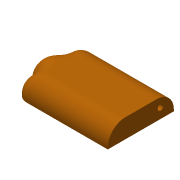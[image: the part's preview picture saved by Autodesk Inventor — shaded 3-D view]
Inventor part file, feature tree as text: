
AUTODESK INVENTOR PART (.ipt)
format: ipt  version: 2016 (Build 200138000, 138)  size: 172,032 bytes
history: native  units: in
note: dims shown in document units (in); Inventor stores cm internally (conversion verified against a paired STEP export)
features: sketch x4, other x3, plane x1
ambient origin geometry x8: Origin, YZ Plane, XZ Plane, XY Plane, X Axis, Y Axis, Z Axis, Center Point
bodies: Solid1 (feature_tree)
feature tree (8):
  other  "P_ankle03_001.ipt"
  other  "Solid1::P_ankle03_001.ipt"
  other  "TaggingFeature1"
  sketch  "Sketch1"  dims[d0=0.3937in]
  sketch  "Sketch3"
  sketch  "Sketch5"
  sketch  "Sketch6"
  plane  "Work Plane1"
